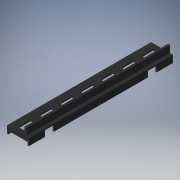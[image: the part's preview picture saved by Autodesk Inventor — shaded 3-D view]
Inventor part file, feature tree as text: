
AUTODESK INVENTOR PART (.ipt)
format: ipt  version: 2019 (Build 230136000, 136)  size: 222,208 bytes
history: native  units: mm
features: other x56, extrude x11, sketch x11
ambient origin geometry x8: Origin, YZ Plane, XZ Plane, XY Plane, X Axis, Y Axis, Z Axis, Center Point
bodies: Solid1 (feature_tree)
feature tree (78):
  extrude  "Extrusion1"  Depth=250.0mm TaperAngle=0.0deg
  extrude  "Extrusion2"  Depth=8.0mm TaperAngle=0.0deg
  extrude  "Extrusion3"  Depth=8.0mm TaperAngle=0.0deg
  extrude  "Extrusion4"  Depth=8.0mm TaperAngle=0.0deg
  extrude  "Extrusion5"  Depth=37.5mm TaperAngle=0.0deg
  extrude  "Extrusion6"  TaperAngle=0.0deg  [1 undecoded]
  extrude  "Extrusion7"  [1 undecoded]
  extrude  "Extrusion8"  [1 undecoded]
  extrude  "Extrusion9"  [1 undecoded]
  extrude  "Extrusion10"  [1 undecoded]
  extrude  "Extrusion11"  [1 undecoded]
  other  "p_XY"
  other  "p_YZ"
  other  "p_ZX"
  other  "p_X"
  other  "p_Y"
  other  "p_Z"
  other  "p_Center"
  other  "p1_XY"
  other  "p1_YZ"
  other  "p1_ZX"
  other  "p1_X"
  other  "p1_Y"
  other  "p1_Z"
  other  "p1_Center"
  other  "p2_XY"
  other  "p2_YZ"
  other  "p2_ZX"
  other  "p2_X"
  other  "p2_Y"
  other  "p2_Z"
  other  "p2_Center"
  other  "p3_XY"
  other  "p3_YZ"
  other  "p3_ZX"
  other  "p3_X"
  other  "p3_Y"
  other  "p3_Z"
  other  "p3_Center"
  other  "p4_XY"
  other  "p4_YZ"
  other  "p4_ZX"
  other  "p4_X"
  other  "p4_Y"
  other  "p4_Z"
  other  "p4_Center"
  other  "p5_XY"
  other  "p5_YZ"
  other  "p5_ZX"
  other  "p5_X"
  other  "p5_Y"
  other  "p5_Z"
  other  "p5_Center"
  other  "p6_XY"
  other  "p6_YZ"
  other  "p6_ZX"
  other  "p6_X"
  other  "p6_Y"
  other  "p6_Z"
  other  "p6_Center"
  other  "p7_XY"
  other  "p7_YZ"
  other  "p7_ZX"
  other  "p7_X"
  other  "p7_Y"
  other  "p7_Z"
  other  "p7_Center"
  sketch  "Sketch_1"  dims[d0=250.0mm d1=0.0mm d2=8.0mm d3=0.0mm]
  sketch  "Sketch_2"  dims[d4=8.0mm d5=0.0mm d6=8.0mm d7=0.0mm]
  sketch  "Sketch_3"  dims[d8=8.0mm d9=0.0mm d10=8.0mm d11=0.0mm]
  sketch  "Sketch_4"  dims[d12=8.0mm d13=0.0mm d14=8.0mm d15=0.0mm]
  sketch  "Sketch_5"  dims[d16=37.5mm d17=0.0mm d18=37.5mm d19=0.0mm]
  sketch  "Sketch_6"  dims[d20=4.7mm d21=0.0mm d22=0.0mm]
  sketch  "Sketch_7"
  sketch  "Sketch_8"
  sketch  "Sketch_10"
  sketch  "Sketch_11"
  sketch  "Sketch_13"
note: 6 required parameter values undecoded (feature->parameter linkage not recoverable at this tier; creation-order binding heuristic only, values carry confidence <= 0.55)
